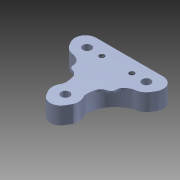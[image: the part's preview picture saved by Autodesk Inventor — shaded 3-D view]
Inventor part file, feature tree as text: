
AUTODESK INVENTOR PART (.ipt)
format: ipt  version: 2011 (Build 150239000, 239)  size: 299,008 bytes
history: native  units: in
note: dims shown in document units (in); Inventor stores cm internally (conversion verified against a paired STEP export)
features: sketch x9, hole x5, extrude x4, fillet x3, other x1, imported_body x1
ambient origin geometry x8: Origin, YZ Plane, XZ Plane, XY Plane, X Axis, Y Axis, Z Axis, Center Point
feature tree (23):
  other  "TricornerHatE"
  imported_body  "Base1"
  hole  "sphere_hole1"  [1 undecoded]
  hole  "sphere_hole2"  [1 undecoded]
  hole  "sphere_hole3"  [1 undecoded]
  hole  "threaded_hole"  [1 undecoded]
  extrude  "Extrusion1"  Depth=0.0787in
  extrude  "Extrusion2"  Depth=0.0787in
  extrude  "Extrusion3"  [1 undecoded]
  fillet  "Fillet1"  [1 undecoded]
  hole  "Hole16"  [1 undecoded]
  extrude  "Extrusion6"  [1 undecoded]
  fillet  "Fillet5"  [1 undecoded]
  fillet  "Fillet6"  [1 undecoded]
  sketch  "Sketch1"  dims[d0=0.0787in d1=0.2362in d2=0.1875in d3=0.0787in d4=90.0deg d5=0.315in d6=0.0in]
  sketch  "Sketch6"  dims[d35=0.0787in d36=0.2362in d37=0.1875in d38=0.0787in d39=90.0deg d40=0.315in d41=0.0in]
  sketch  "Sketch7"  dims[d42=0.0787in d43=0.2362in d44=0.1875in d45=0.0787in d46=90.0deg d47=0.315in d48=0.0in]
  sketch  "Sketch9"  dims[d56=0.0617in d57=0.2362in d58=0.1575in d59=0.0787in d60=90.0deg d61=0.1181in d62=0.8108in d63=0.315in]
  sketch  "Sketch10"  dims[d64=0.1378in d65=0.0in d67=0.1378in d68=0.0in]
  sketch  "Sketch11"  dims[d69=0.1378in d70=0.0in d84=0.0787in]
  sketch  "Sketch12"  dims[d91=0.1575in d93=0.1181in d94=0.0in]
  sketch  "Sketch18"  dims[d97=0.1378in d98=0.0787in]
  sketch  "Sketch20"  dims[d114=0.2756in d115=0.0465in d116=0.2362in d117=0.1575in d118=0.0787in d119=90.0deg d120=0.1575in d121=0.8108in d122=0.0787in]
note: 10 required parameter values undecoded (feature->parameter linkage not recoverable at this tier; creation-order binding heuristic only, values carry confidence <= 0.55)
